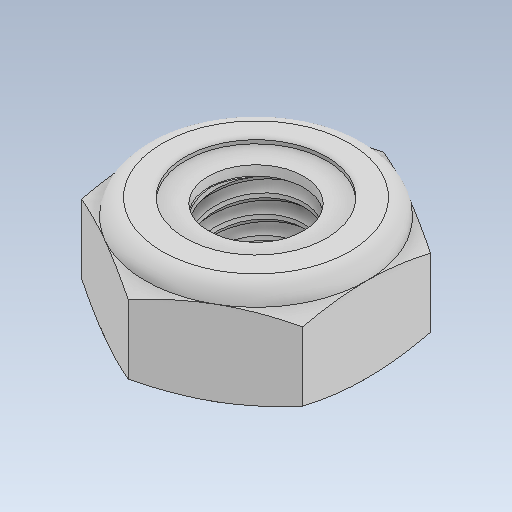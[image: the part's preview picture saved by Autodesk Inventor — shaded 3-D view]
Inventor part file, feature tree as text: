
AUTODESK INVENTOR PART (.ipt)
format: ipt  version: 2020 (Build 240168000, 168)  size: 285,184 bytes
history: native  units: in
note: dims shown in document units (in); Inventor stores cm internally (conversion verified against a paired STEP export)
features: other x1, revolve x1
ambient origin geometry x8: Origin, YZ Plane, XZ Plane, XY Plane, X Axis, Y Axis, Z Axis, Center Point
bodies: Solid1 (feature_tree), Solid2 (feature_tree)
feature tree (2):
  other  "Cut-Revolve4"
  revolve  "Revolve2"  [1 undecoded]
note: 1 required parameter value undecoded (feature->parameter linkage not recoverable at this tier; creation-order binding heuristic only, values carry confidence <= 0.55)
